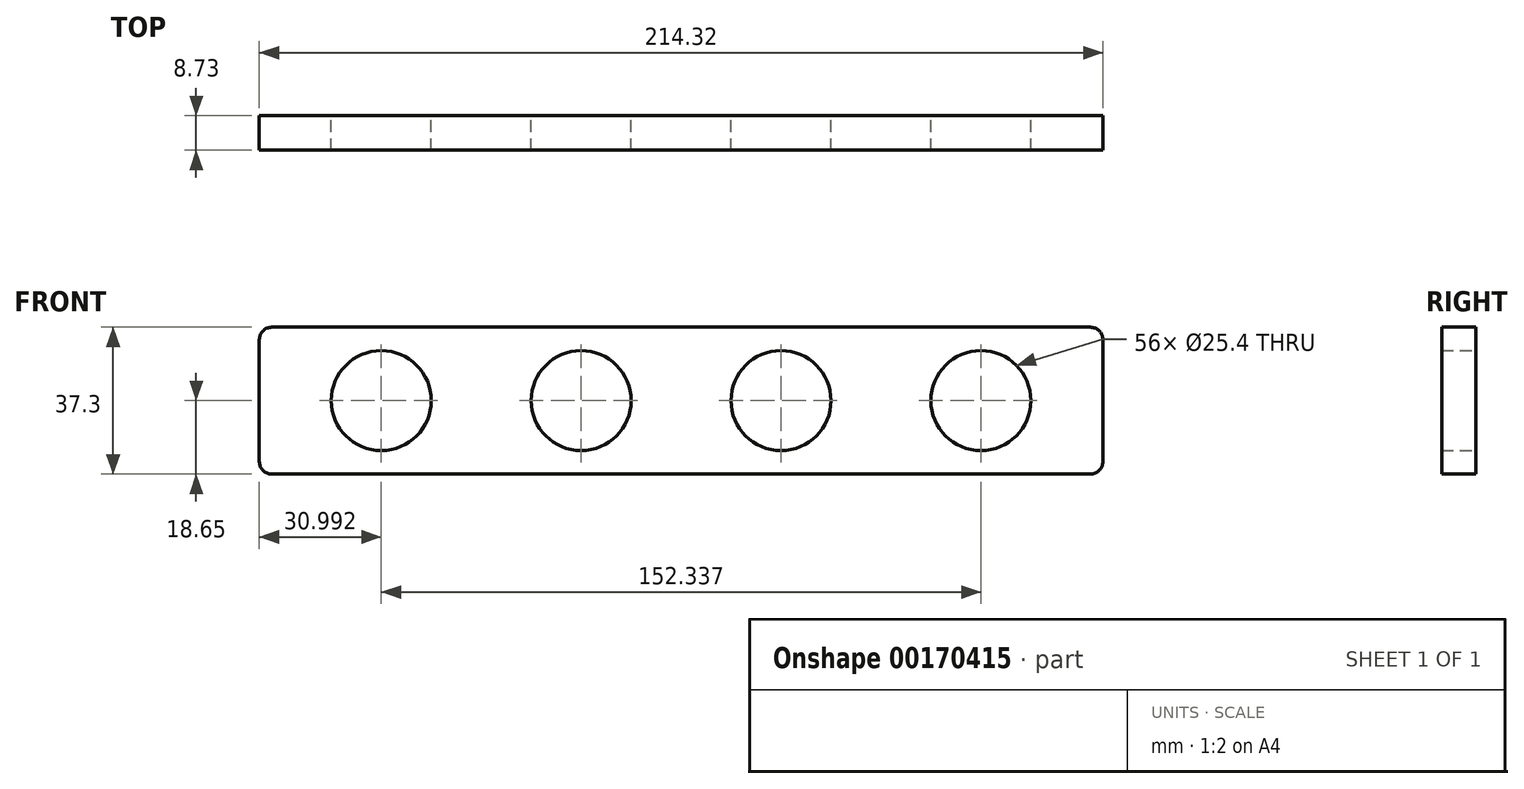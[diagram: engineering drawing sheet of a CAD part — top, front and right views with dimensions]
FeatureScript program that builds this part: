
annotation { "Feature Type Name" : "Feature", "Feature Type Description" : "" }
export const myFeature = defineFeature(function(context is Context, id is Id, definition is map)
    precondition{}
    {
        {
            var Q0;
            Q0=qCreatedBy(makeId("Front.planeOp"),FACE);
            var sketch = newSketch(context, id + "F0", { "sketchPlane" : qUnion([Q0])});
            skLineSegment(sketch, "E0.bottom", {"start": v(-103.98, 18.65) * mm, "end": v(103.98, 18.65) * mm});
            skLineSegment(sketch, "E0.top", {"start": v(-103.98, -18.65) * mm, "end": v(103.98, -18.65) * mm});
            skLineSegment(sketch, "E0.left", {"start": v(-107.16, 15.48) * mm, "end": v(-107.16, -15.48) * mm});
            skLineSegment(sketch, "E0.right", {"start": v(107.16, 15.48) * mm, "end": v(107.16, -15.48) * mm});
            skPoint(sketch, "E0.middle", {"position": v(0, 0) * mm});
            skPoint(sketch, "E1.visualSharp", {"position": v(-107.16, 18.65) * mm});
            skArc(sketch, "E1.filletArc", {"start": v(-103.98, 18.65) * mm, "mid": v(-106.23, 17.72) * mm, "end": v(-107.16, 15.48) * mm});
            skPoint(sketch, "E2.visualSharp", {"position": v(-107.16, -18.65) * mm});
            skArc(sketch, "E2.filletArc", {"start": v(-107.16, -15.48) * mm, "mid": v(-106.23, -17.72) * mm, "end": v(-103.98, -18.65) * mm});
            skPoint(sketch, "E3.visualSharp", {"position": v(107.16, -18.65) * mm});
            skArc(sketch, "E3.filletArc", {"start": v(103.98, -18.65) * mm, "mid": v(106.23, -17.72) * mm, "end": v(107.16, -15.48) * mm});
            skPoint(sketch, "E4.visualSharp", {"position": v(107.16, 18.65) * mm});
            skArc(sketch, "E4.filletArc", {"start": v(107.16, 15.48) * mm, "mid": v(106.23, 17.72) * mm, "end": v(103.98, 18.65) * mm});
            skLineSegment(sketch, "E5", {"start": v(-107.16, 0) * mm, "end": v(107.16, 0) * mm, "construction": true});
            skCircle(sketch, "E6", {"center": v(-76.17, 0) * mm, "radius": 12.7 * mm});
            skCircle(sketch, "E7", {"center": v(-25.39, 0) * mm, "radius": 12.7 * mm});
            skCircle(sketch, "E8", {"center": v(25.39, 0) * mm, "radius": 12.7 * mm});
            skCircle(sketch, "E9", {"center": v(76.17, 0) * mm, "radius": 12.7 * mm});
            skSolve(sketch);
        }
        {
            var Q0;
            Q0=makeQuery(id+"F0.imprint","IMPRINT",FACE,{"disambiguationData":[TD([[makeQuery(id+"F0.imprint","IMPRINT",EDGE,{"derivedFrom":sQuery(id+"F0.wireOp",EDGE,"E0.bottom")}),-1.0]])]});
            extrude(context, id + "F1", {"entities" : qUnion([Q0]), "depth" : 8.73 * mm});
        }
    });
